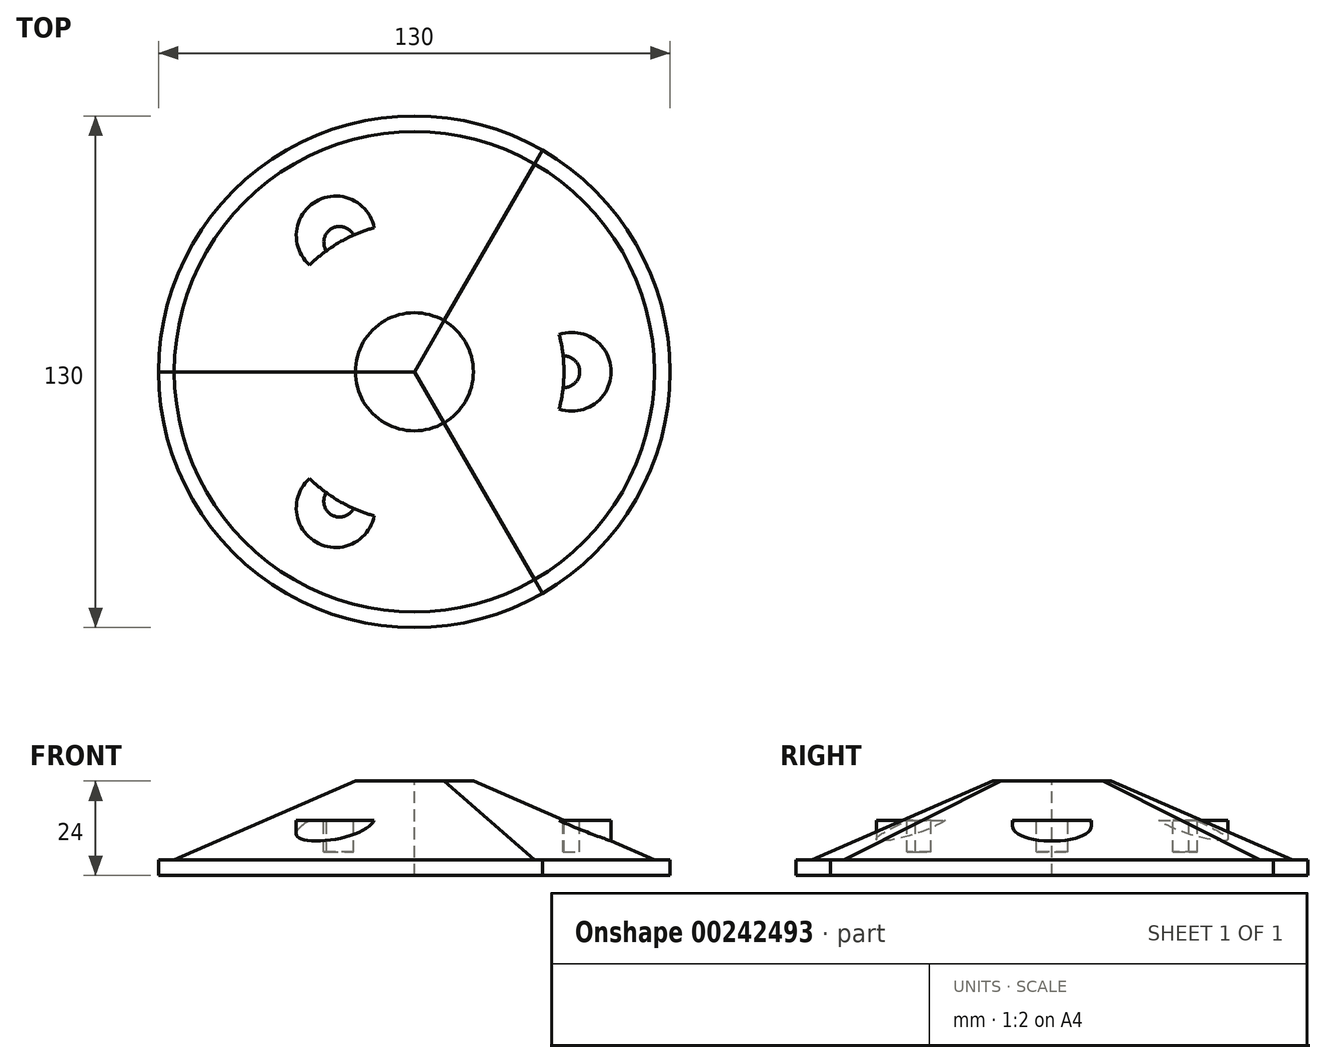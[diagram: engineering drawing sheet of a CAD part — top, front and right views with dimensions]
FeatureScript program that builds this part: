
annotation { "Feature Type Name" : "Feature", "Feature Type Description" : "" }
export const myFeature = defineFeature(function(context is Context, id is Id, definition is map)
    precondition{}
    {
        {
            var Q0;
            Q0=qCreatedBy(makeId("Front.planeOp"),FACE);
            var sketch = newSketch(context, id + "F0", { "sketchPlane" : qUnion([Q0])});
            skLineSegment(sketch, "E0", {"start": v(-65, 0) * mm, "end": v(65, 0) * mm});
            skLineSegment(sketch, "E1", {"start": v(0, 0) * mm, "end": v(0, 24) * mm});
            skLineSegment(sketch, "E2", {"start": v(-15, 24) * mm, "end": v(15, 24) * mm});
            skLineSegment(sketch, "E3", {"start": v(-65, 0) * mm, "end": v(-65, 4) * mm});
            skLineSegment(sketch, "E4", {"start": v(-65, 4) * mm, "end": v(-61, 4) * mm});
            skLineSegment(sketch, "E5", {"start": v(-61, 4) * mm, "end": v(-15, 24) * mm});
            skLineSegment(sketch, "E6.MirrorCS", {"start": v(61, 4) * mm, "end": v(15, 24) * mm});
            skLineSegment(sketch, "E7.MirrorCS", {"start": v(65, 4) * mm, "end": v(61, 4) * mm});
            skLineSegment(sketch, "E8.MirrorCS", {"start": v(65, 0) * mm, "end": v(65, 4) * mm});
            skLineSegment(sketch, "E9.0", {"start": v(-14.17, 20) * mm, "end": v(15, 20) * mm});
            skLineSegment(sketch, "E9.1", {"start": v(-60.17, 0) * mm, "end": v(-14.17, 20) * mm});
            skLineSegment(sketch, "E10.MirrorCS", {"start": v(60.17, 0) * mm, "end": v(14.17, 20) * mm});
            skLineSegment(sketch, "E11", {"start": v(0, 38.15) * mm, "end": v(40, 38.15) * mm});
            skLineSegment(sketch, "E12", {"start": v(40, 38.15) * mm, "end": v(40, -51.58) * mm, "construction": true});
            skSolve(sketch);
        }
        {
            var Q0;
            {var subQ3=sQuery(id+"F0.wireOp",EDGE,"E9.1");Q0=makeQuery(id+"F0.imprint","IMPRINT",FACE,{"disambiguationData":[TD([[makeQuery(id+"F0.imprint","IMPRINT",EDGE,{"derivedFrom":subQ3}),-1.0]])]});}
            var Q1;
            {var subQ0=sQuery(id+"F0.wireOp",EDGE,"E3");Q1=makeQuery(id+"F0.imprint","IMPRINT",FACE,{"disambiguationData":[TD([[makeQuery(id+"F0.imprint","IMPRINT",EDGE,{"derivedFrom":subQ0}),-1.0]])]});}
            var Q2;
            Q2=sQuery(id+"F0.wireOp",EDGE,"E1");
            revolve(context, id + "F1", {"entities" : qUnion([Q0, Q1]), "axis" : qUnion([Q2]), "revolveType" : RevolveType.ONE_DIRECTION, "angle" : 120 * degree});
        }
        {
            var Q0;
            Q0=makeQuery(id+"F1.opRevolve","SWEPT_FACE",FACE,{"disambiguationData":[OSD([sQuery(id+"F0.wireOp",EDGE,"E0")])]});
            var sketch = newSketch(context, id + "F2", { "sketchPlane" : qUnion([Q0])});
            skLineSegment(sketch, "E13.0.0", {"start": v(-65, 0) * mm, "end": v(0, 0) * mm});
            skLineSegment(sketch, "E13.0.1", {"start": v(0, 0) * mm, "end": v(32.5, 56.3) * mm});
            skArc(sketch, "E13.0.2", {"start": v(32.5, 56.3) * mm, "mid": v(-32.5, 56.3) * mm, "end": v(-65, 0) * mm});
            skLineSegment(sketch, "E14", {"start": v(0, 0) * mm, "end": v(-32.5, 56.3) * mm, "construction": true});
            skLineSegment(sketch, "E15", {"start": v(0, 0) * mm, "end": v(-20, 34.64) * mm});
            skCircle(sketch, "E16", {"center": v(-20, 34.64) * mm, "radius": 10 * mm});
            skSolve(sketch);
        }
        {
            var Q0;
            Q0=makeQuery(id+"F2.imprint","IMPRINT",FACE,{"disambiguationData":[TD([[makeQuery(id+"F2.imprint","IMPRINT",EDGE,{"derivedFrom":sQuery(id+"F2.wireOp",EDGE,"E16")}),1.0]])]});
            extrude(context, id + "F3", {"entities" : qUnion([Q0]), "operationType" : NewBodyOperationType.ADD, "oppositeDirection" : true, "depth" : 14 * mm});
        }
        {
            var Q0;
            Q0=makeQuery(id+"F3.opExtrude","CAP_FACE",FACE,{"disambiguationData":[OSD([sQuery(id+"F2.wireOp",EDGE,"E16")])],"isStart":false});
            var sketch = newSketch(context, id + "F4", { "sketchPlane" : qUnion([Q0])});
            skPoint(sketch, "E17.0", {"position": v(-19, -32.9) * mm});
            skCircle(sketch, "E18", {"center": v(-19, -32.9) * mm, "radius": 4 * mm});
            skArc(sketch, "E19.0", {"start": v(-26.6, -27.13) * mm, "mid": v(-19, -32.9) * mm, "end": v(-10.2, -36.6) * mm});
            skSolve(sketch);
        }
        {
            var Q0;
            {var subQ0=sQuery(id+"F4.wireOp",EDGE,"E19.0");var subQ1=sQuery(id+"F4.wireOp",EDGE,"E18");var subQ2=makeQuery(id+"F4.imprint","INTERSECT",VERTEX,{"disambiguationData":[OD(0.0)],"derivedFrom":[subQ1,subQ0]});Q0=makeQuery(id+"F4.imprint","IMPRINT",FACE,{"disambiguationData":[TD([[makeQuery(id+"F4.imprint","IMPRINT",EDGE,{"disambiguationData":[TD([[subQ2,1.0]])],"derivedFrom":subQ1}),1.0]])]});}
            extrude(context, id + "F5", {"entities" : qUnion([Q0]), "operationType" : NewBodyOperationType.REMOVE, "oppositeDirection" : true, "depth" : 8 * mm});
        }
        {
            var Q0;
            Q0=makeQuery(id+"F1.opRevolve","SWEPT_BODY",BODY,{"disambiguationData":[OSD([sQuery(id+"F0.wireOp",EDGE,"E0"),sQuery(id+"F0.wireOp",EDGE,"E1"),sQuery(id+"F0.wireOp",EDGE,"E2"),sQuery(id+"F0.wireOp",EDGE,"E3"),sQuery(id+"F0.wireOp",EDGE,"E4"),sQuery(id+"F0.wireOp",EDGE,"E5")])]});
            var Q1;
            Q1=makeQuery(id+"F1.opRevolve","CAP_EDGE",EDGE,{"disambiguationData":[OSD([sQuery(id+"F0.wireOp",EDGE,"E1")])],"isStart":true});
            circularPattern(context, id + "F6", {"entities" : qUnion([Q0]), "axis" : qUnion([Q1]), "angle" : 360 * degree, "instanceCount" : 3, "equalSpace" : true});
        }
    });
